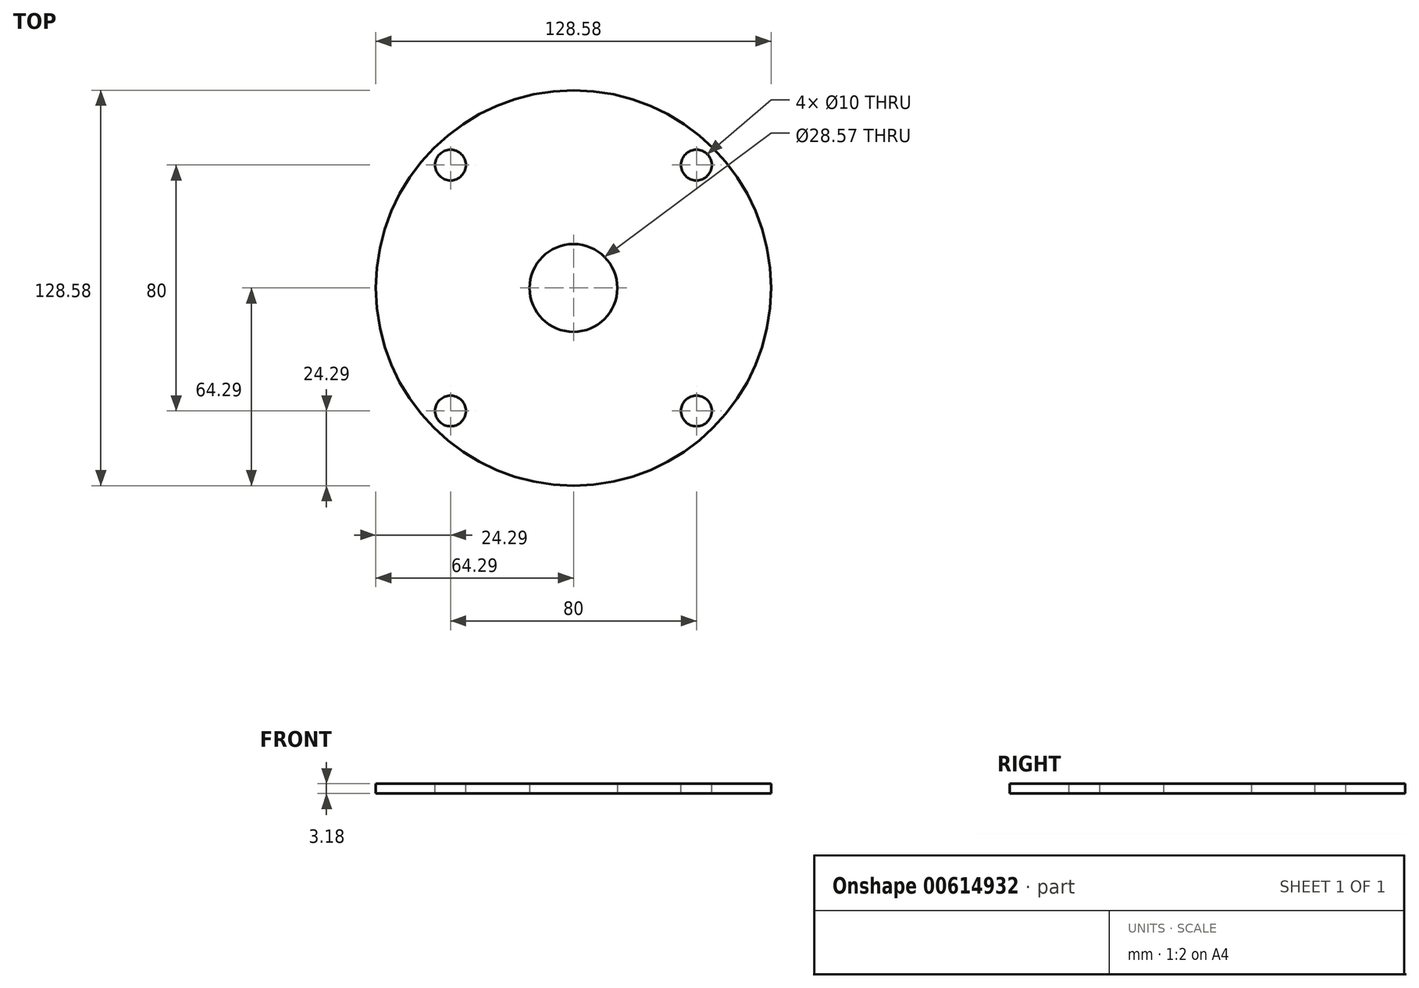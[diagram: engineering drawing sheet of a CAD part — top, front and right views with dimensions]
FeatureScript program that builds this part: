
annotation { "Feature Type Name" : "Feature", "Feature Type Description" : "" }
export const myFeature = defineFeature(function(context is Context, id is Id, definition is map)
    precondition{}
    {
        {
            var Q0;
            Q0=qCreatedBy(makeId("Top.planeOp"),FACE);
            var sketch = newSketch(context, id + "F0", { "sketchPlane" : qUnion([Q0])});
            skCircle(sketch, "E0", {"center": v(0, 0) * mm, "radius": 14.29 * mm});
            skCircle(sketch, "E1", {"center": v(0, 0) * mm, "radius": 64.29 * mm});
            skLineSegment(sketch, "E2", {"start": v(14.29, 0) * mm, "end": v(64.29, 0) * mm});
            skSolve(sketch);
        }
        {
            var Q0;
            Q0=qSketchRegion(id+"F0",true);
            extrude(context, id + "F1", {"entities" : qUnion([Q0]), "depth" : 0.12 * 25.4 * mm, "offsetDistance" : 25 * mm});
        }
        {
            var Q0;
            Q0=makeQuery(id+"F1.opExtrude","CAP_FACE",FACE,{"disambiguationData":[OSD([sQuery(id+"F0.wireOp",EDGE,"E0"),sQuery(id+"F0.wireOp",EDGE,"E1")])],"isStart":false});
            var sketch = newSketch(context, id + "F2", { "sketchPlane" : qUnion([Q0])});
            skLineSegment(sketch, "E3.bottom", {"start": v(45.5, 45.42) * mm, "end": v(-45.5, 45.42) * mm});
            skLineSegment(sketch, "E3.top", {"start": v(45.5, -45.42) * mm, "end": v(-45.5, -45.42) * mm});
            skLineSegment(sketch, "E3.left", {"start": v(45.5, 45.42) * mm, "end": v(45.5, -45.42) * mm});
            skLineSegment(sketch, "E3.right", {"start": v(-45.5, 45.42) * mm, "end": v(-45.5, -45.42) * mm});
            skPoint(sketch, "E3.middle", {"position": v(0, 0) * mm});
            skLineSegment(sketch, "E4.bottom", {"start": v(40, 40) * mm, "end": v(-40, 40) * mm});
            skLineSegment(sketch, "E4.top", {"start": v(40, -40) * mm, "end": v(-40, -40) * mm});
            skLineSegment(sketch, "E4.left", {"start": v(40, 40) * mm, "end": v(40, -40) * mm});
            skLineSegment(sketch, "E4.right", {"start": v(-40, 40) * mm, "end": v(-40, -40) * mm});
            skCircle(sketch, "E5", {"center": v(-40, 40) * mm, "radius": 5 * mm});
            skCircle(sketch, "E6.MirrorC", {"center": v(40, 40) * mm, "radius": 5 * mm});
            skCircle(sketch, "E7.MirrorC", {"center": v(40, -40) * mm, "radius": 5 * mm});
            skCircle(sketch, "E8.MirrorC", {"center": v(-40, -40) * mm, "radius": 5 * mm});
            skSolve(sketch);
        }
        {
            var Q0;
            {var subQ0=sQuery(id+"F2.wireOp",EDGE,"E4.right");var subQ1=sQuery(id+"F2.wireOp",EDGE,"E4.bottom");var subQ2=makeQuery(id+"F2.imprint","INTERSECT",VERTEX,{"derivedFrom":[subQ1,subQ0]});Q0=makeQuery(id+"F2.imprint","IMPRINT",FACE,{"disambiguationData":[TD([[makeQuery(id+"F2.imprint","IMPRINT",EDGE,{"disambiguationData":[TD([[subQ2,1.0]])],"derivedFrom":subQ1}),1.0]])]});}
            var Q1;
            {var subQ0=sQuery(id+"F2.wireOp",EDGE,"E4.right");var subQ1=sQuery(id+"F2.wireOp",EDGE,"E4.bottom");var subQ2=makeQuery(id+"F2.imprint","INTERSECT",VERTEX,{"derivedFrom":[subQ1,subQ0]});Q1=makeQuery(id+"F2.imprint","IMPRINT",FACE,{"disambiguationData":[TD([[makeQuery(id+"F2.imprint","IMPRINT",EDGE,{"disambiguationData":[TD([[subQ2,1.0]])],"derivedFrom":subQ1}),-1.0]])]});}
            var Q2;
            {var subQ0=sQuery(id+"F2.wireOp",EDGE,"E4.left");var subQ1=sQuery(id+"F2.wireOp",EDGE,"E4.bottom");var subQ2=makeQuery(id+"F2.imprint","INTERSECT",VERTEX,{"derivedFrom":[subQ1,subQ0]});Q2=makeQuery(id+"F2.imprint","IMPRINT",FACE,{"disambiguationData":[TD([[makeQuery(id+"F2.imprint","IMPRINT",EDGE,{"disambiguationData":[TD([[subQ2,-1.0]])],"derivedFrom":subQ1}),1.0]])]});}
            var Q3;
            {var subQ0=sQuery(id+"F2.wireOp",EDGE,"E4.left");var subQ1=sQuery(id+"F2.wireOp",EDGE,"E4.bottom");var subQ2=makeQuery(id+"F2.imprint","INTERSECT",VERTEX,{"derivedFrom":[subQ1,subQ0]});Q3=makeQuery(id+"F2.imprint","IMPRINT",FACE,{"disambiguationData":[TD([[makeQuery(id+"F2.imprint","IMPRINT",EDGE,{"disambiguationData":[TD([[subQ2,-1.0]])],"derivedFrom":subQ1}),-1.0]])]});}
            var Q4;
            {var subQ0=sQuery(id+"F2.wireOp",EDGE,"E4.left");var subQ1=sQuery(id+"F2.wireOp",EDGE,"E4.top");var subQ2=makeQuery(id+"F2.imprint","INTERSECT",VERTEX,{"derivedFrom":[subQ1,subQ0]});Q4=makeQuery(id+"F2.imprint","IMPRINT",FACE,{"disambiguationData":[TD([[makeQuery(id+"F2.imprint","IMPRINT",EDGE,{"disambiguationData":[TD([[subQ2,-1.0]])],"derivedFrom":subQ1}),1.0]])]});}
            var Q5;
            {var subQ0=sQuery(id+"F2.wireOp",EDGE,"E4.left");var subQ1=sQuery(id+"F2.wireOp",EDGE,"E4.top");var subQ2=makeQuery(id+"F2.imprint","INTERSECT",VERTEX,{"derivedFrom":[subQ1,subQ0]});Q5=makeQuery(id+"F2.imprint","IMPRINT",FACE,{"disambiguationData":[TD([[makeQuery(id+"F2.imprint","IMPRINT",EDGE,{"disambiguationData":[TD([[subQ2,-1.0]])],"derivedFrom":subQ1}),-1.0]])]});}
            var Q6;
            {var subQ0=sQuery(id+"F2.wireOp",EDGE,"E4.right");var subQ1=sQuery(id+"F2.wireOp",EDGE,"E4.top");var subQ2=makeQuery(id+"F2.imprint","INTERSECT",VERTEX,{"derivedFrom":[subQ1,subQ0]});Q6=makeQuery(id+"F2.imprint","IMPRINT",FACE,{"disambiguationData":[TD([[makeQuery(id+"F2.imprint","IMPRINT",EDGE,{"disambiguationData":[TD([[subQ2,1.0]])],"derivedFrom":subQ1}),1.0]])]});}
            var Q7;
            {var subQ0=sQuery(id+"F2.wireOp",EDGE,"E4.right");var subQ1=sQuery(id+"F2.wireOp",EDGE,"E4.top");var subQ2=makeQuery(id+"F2.imprint","INTERSECT",VERTEX,{"derivedFrom":[subQ1,subQ0]});Q7=makeQuery(id+"F2.imprint","IMPRINT",FACE,{"disambiguationData":[TD([[makeQuery(id+"F2.imprint","IMPRINT",EDGE,{"disambiguationData":[TD([[subQ2,1.0]])],"derivedFrom":subQ1}),-1.0]])]});}
            extrude(context, id + "F3", {"entities" : qUnion([Q0, Q1, Q2, Q3, Q4, Q5, Q6, Q7]), "operationType" : NewBodyOperationType.REMOVE, "oppositeDirection" : true, "depth" : 25 * mm, "offsetDistance" : 25 * mm});
        }
    });
